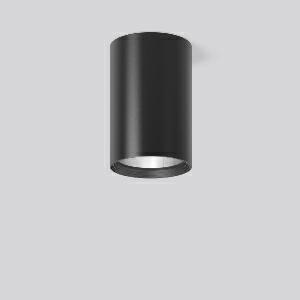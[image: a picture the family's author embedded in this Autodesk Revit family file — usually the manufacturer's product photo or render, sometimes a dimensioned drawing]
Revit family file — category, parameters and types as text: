
# Revit family: heledon_maxi_a_931219_003_76_ac0f
name_source: partatom
category: Lighting Fixtures
units: mm (PartAtom-declared; Revit-internal decimal feet)

## family parameters
Cut with Voids When Loaded = No
Host = Face
Light Source = No
Part Type = Normal
Room Calculation Point = No
Round Connector Dimension = Use Diameter
Shared = No

## types (1)
- HELEDON maxi A (1 x LED Modul 930, 3250 lm, 3000)
    Apparent Load = 25 VA
    Approval mark = CE
    CIE Flux Codes = 97 100 100 100 100
    Color Rendering = 90
    Color Temperature = 3000
    Default Elevation = 1800 mm
    Description = Series: HELEDON maxi
Cylindrical surface-mounted downlight. Housing: die-cast aluminium, powder-coated. Internal ceiling frame polycarbonate with bayonet mounting. Black plastic ring and recessed LED to prevent glare from the side. Optical assembly with reflector made of MIRO-Silver with 98% total light reflection for outstanding efficiency - can be changed without tools. Best colour rendering index Ra>90. Suitable for Ceiling mounting. Easy installation with a separate ceiling frame with bayonet mounting and plug connection. Driver integrated. Connected via plug-in connector. High quality converter without flickering and stroboscopic effect. The following accessories can be mounted without use of tools: interchangeable lenses, decorative glasses, honeycomb louvre, clear and frosted diffusers, white interchangeable plastic ring. 
Colour: deep black, matt (RAL 9005)
Diameter: 123 mm
Height: 183 mm
Lamp: LED
Socket: without socket
Colour temperature: 3000K
Colour rendering index (CRI): 92
System power: 25 W
Rated luminous flux: 3250 lm
Luminous efficiency: 130 lm/W
Control gear: Converter, dimmable, DALI
Protection class: I
Type of protection: IP 20
    Height = 183 mm
    Lamp = 1 x LED Modul 930
    Lamp Light Flux = 3250 lm
    Lamp count = 1
    Length = 123 mm
    Lifetime = 50000 h
    Luminous efficacy = 130 lm/W
    Manufacturer = RZB
    ModVariant = No
    Model = 931219.003.76
    Mounting Place = Ceiling
    Mounting Type = Surface mounted
    Number of Poles = 1
    OnlyDefault = Yes
    Power Factor = 1
    Product Name = HELEDON maxi A
    Product group = Surface mounted downlights
    ProductGroupID = 302
    Protection Class = Protection class I
    Protection Degree = IP 20
    RLX_Detail_Level = 1
    RLX_Emergency_Light_Flux = 0 lm
    RLX_Emergency_Type = 0
    RLX_Emergency_Type_DB = No
    RlxData = <blob elided: 96905 chars, md5=03b3b838>
    Socket = socket
    Standby Power = 0 W
    System Light Flux = 3250 lm
    System Power = 25 W
    Type Comments = Product without accessories
    Type Image = 931192.003.jpg
    URL = http://relux.com
    VarID = ---
    Voltage = 230 V
    Voltage Range = 220-240 V
    Weight = 0.00 kg
    Width = 0 mm  [stored 0 ft]

note: [stored X ft] marks values corroborated as IEEE doubles in the binary element streams (Revit-internal decimal feet)

## geometry (parser evidence)
native form markers: Blend x4, Sweep x11
no freeform markers — native parametric forms only
